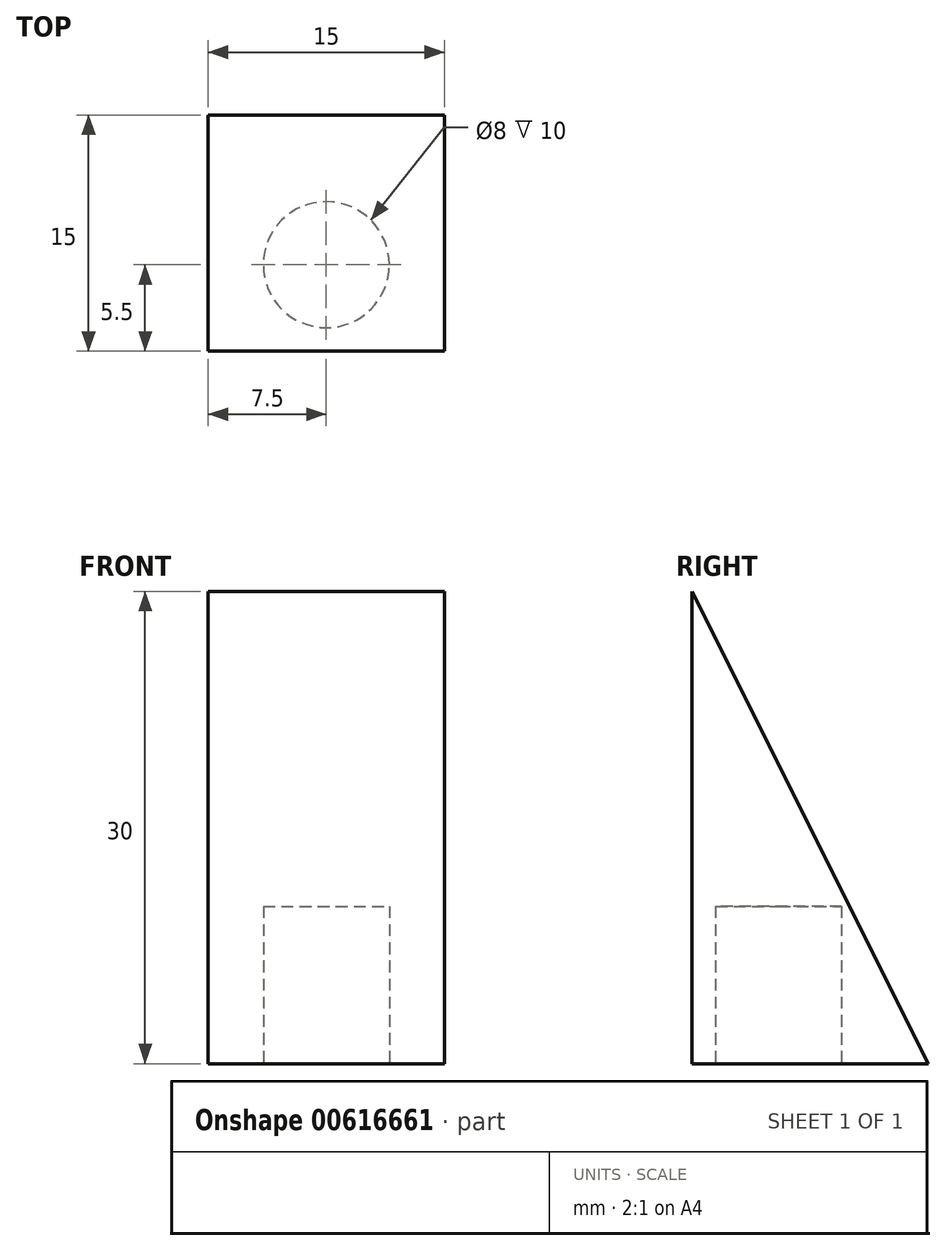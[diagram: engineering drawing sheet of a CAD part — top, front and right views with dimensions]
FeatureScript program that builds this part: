
annotation { "Feature Type Name" : "Feature", "Feature Type Description" : "" }
export const myFeature = defineFeature(function(context is Context, id is Id, definition is map)
    precondition{}
    {
        {
            var Q0;
            Q0=qCreatedBy(makeId("Top.planeOp"),FACE);
            var sketch = newSketch(context, id + "F0", { "sketchPlane" : qUnion([Q0])});
            skLineSegment(sketch, "E0.bottom", {"start": v(0, 0) * mm, "end": v(15, 0) * mm});
            skLineSegment(sketch, "E0.top", {"start": v(0, 15) * mm, "end": v(15, 15) * mm});
            skLineSegment(sketch, "E0.left", {"start": v(0, 0) * mm, "end": v(0, 15) * mm});
            skLineSegment(sketch, "E0.right", {"start": v(15, 0) * mm, "end": v(15, 15) * mm});
            skSolve(sketch);
        }
        {
            var Q0;
            Q0 = qSketchRegion(id + "F0", true);
            extrude(context, id + "F1", {"entities" : qUnion([Q0]), "depth" : 30 * mm, "offsetDistance" : 25 * mm});
        }
        {
            var Q0;
            Q0=makeQuery(id+"F1.opExtrude","SWEPT_FACE",FACE,{"disambiguationData":[OSD([sQuery(id+"F0.wireOp",EDGE,"E0.right")])]});
            var sketch = newSketch(context, id + "F2", { "sketchPlane" : qUnion([Q0])});
            skLineSegment(sketch, "E1", {"start": v(0, 30) * mm, "end": v(15, 0) * mm});
            skSolve(sketch);
        }
        {
            var Q0;
            Q0 = qSketchRegion(id + "F2", true);
            var Q1;
            {var subQ0=sQuery(id+"F2.wireOp",EDGE,"5zLjUCzS-XpCl-fitW-zR6f-8JhglHtJCUtx");Q1=makeQuery(id+"F2.imprint","IMPRINT",FACE,{"disambiguationData":[TD([[makeQuery(id+"F2.imprint","IMPRINT",EDGE,{"derivedFrom":subQ0}),1.0]])]});}
            var Q2;
            {var subQ0=sQuery(id+"F2.wireOp",EDGE,"YGuy0iGo-l7Ed-reuT-2kUH-nzfo1ZSNDrSR");Q2=makeQuery(id+"F2.imprint","IMPRINT",FACE,{"disambiguationData":[TD([[makeQuery(id+"F2.imprint","IMPRINT",EDGE,{"derivedFrom":subQ0}),-1.0]])]});}
            var Q3;
            Q3=makeQuery(id+"F2.imprint","IMPRINT",FACE,{"disambiguationData":[TD([[makeQuery(id+"F2.imprint","IMPRINT",EDGE,{"derivedFrom":sQuery(id+"F2.wireOp",EDGE,"E1")}),1.0]])]});
            extrude(context, id + "F3", {"entities" : qUnion([Q0, Q1, Q2, Q3]), "operationType" : NewBodyOperationType.REMOVE, "oppositeDirection" : true, "depth" : 25 * mm, "offsetDistance" : 25 * mm});
        }
        {
            var Q0;
            Q0=makeQuery(id+"F1.opExtrude","CAP_FACE",FACE,{"disambiguationData":[OSD([sQuery(id+"F0.wireOp",EDGE,"E0.bottom"),sQuery(id+"F0.wireOp",EDGE,"E0.top"),sQuery(id+"F0.wireOp",EDGE,"E0.left"),sQuery(id+"F0.wireOp",EDGE,"E0.right")])],"isStart":true});
            var sketch = newSketch(context, id + "F4", { "sketchPlane" : qUnion([Q0])});
            skLineSegment(sketch, "E2", {"start": v(15, 0) * mm, "end": v(0, -15) * mm, "construction": true});
            skLineSegment(sketch, "E3", {"start": v(0, 0) * mm, "end": v(15, -15) * mm, "construction": true});
            skLineSegment(sketch, "E4", {"start": v(7.5, -7.5) * mm, "end": v(7.5, -5.5) * mm, "construction": true});
            skCircle(sketch, "E5", {"center": v(7.5, -5.5) * mm, "radius": 4 * mm});
            skSolve(sketch);
        }
        {
            var Q0;
            Q0 = qSketchRegion(id + "F4", true);
            extrude(context, id + "F5", {"entities" : qUnion([Q0]), "operationType" : NewBodyOperationType.REMOVE, "oppositeDirection" : true, "depth" : 10 * mm, "offsetDistance" : 25 * mm});
        }
    });
